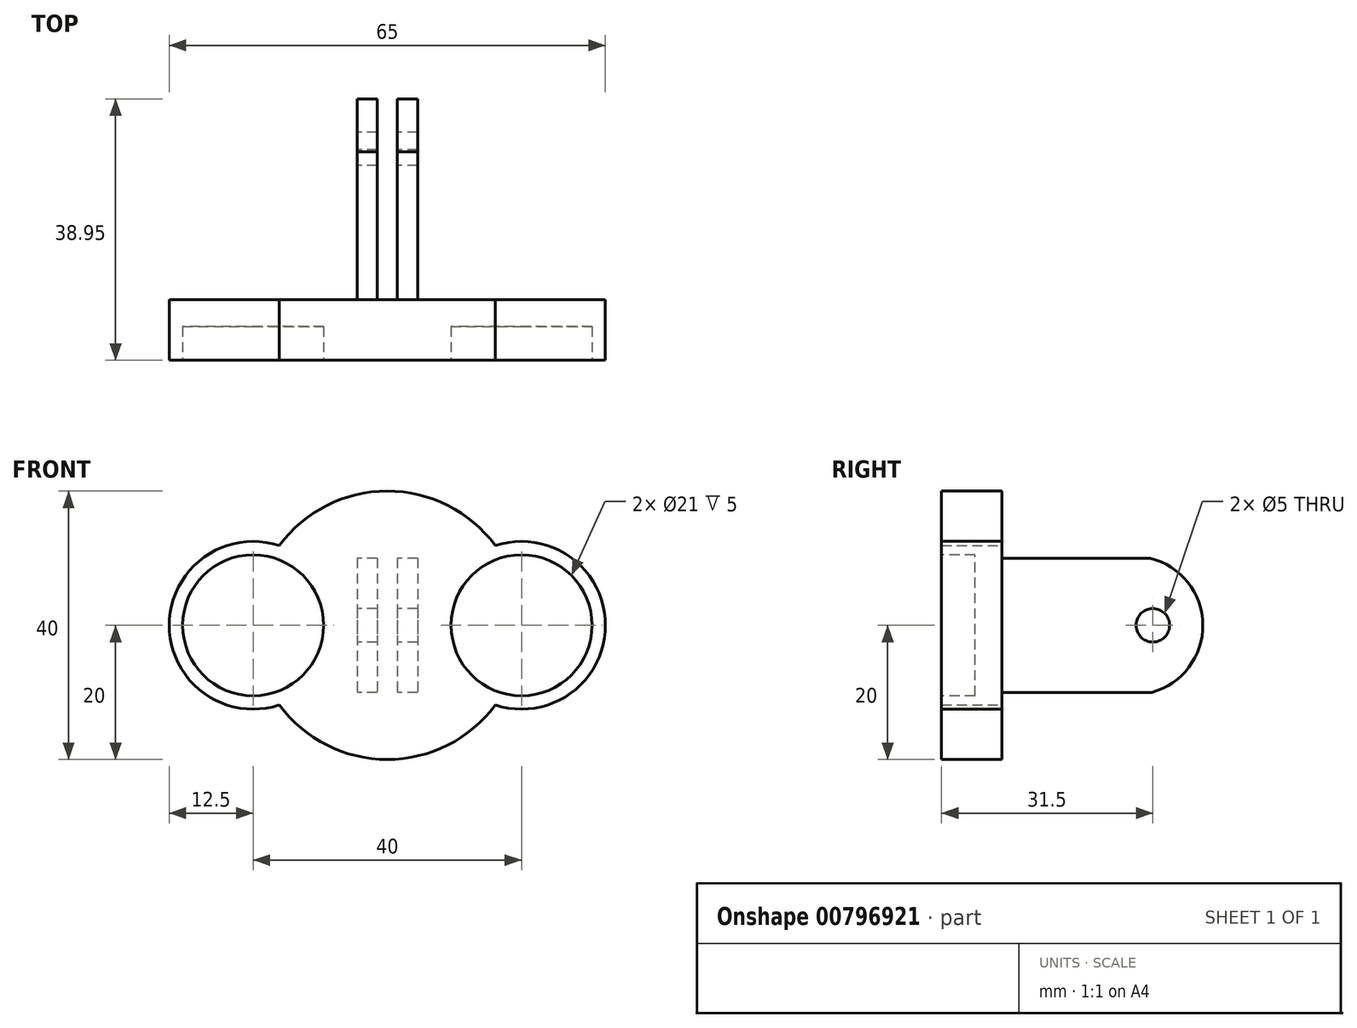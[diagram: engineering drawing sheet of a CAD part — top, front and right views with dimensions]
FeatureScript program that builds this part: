
annotation { "Feature Type Name" : "Feature", "Feature Type Description" : "" }
export const myFeature = defineFeature(function(context is Context, id is Id, definition is map)
    precondition{}
    {
        {
            var Q0;
            Q0=qCreatedBy(makeId("Front.planeOp"),FACE);
            var sketch = newSketch(context, id + "F0", { "sketchPlane" : qUnion([Q0])});
            skCircle(sketch, "E0", {"center": v(0, 0) * mm, "radius": 20 * mm});
            skCircle(sketch, "E1", {"center": v(-20, 0) * mm, "radius": 12.5 * mm});
            skCircle(sketch, "E2", {"center": v(20, 0) * mm, "radius": 12.5 * mm});
            skSolve(sketch);
        }
        {
            var Q0;
            Q0=qSketchRegion(id+"F0",true);
            extrude(context, id + "F1", {"entities" : qUnion([Q0]), "depth" : 9 * mm, "offsetDistance" : 25 * mm});
        }
        {
            var Q0;
            Q0=makeQuery(id+"F1.opExtrude","CAP_FACE",FACE,{"disambiguationData":[OSD([sQuery(id+"F0.wireOp",EDGE,"E0")])],"isStart":true});
            var sketch = newSketch(context, id + "F2", { "sketchPlane" : qUnion([Q0])});
            skLineSegment(sketch, "E3.bottom", {"start": v(-4.5, 10) * mm, "end": v(-1.5, 10) * mm});
            skLineSegment(sketch, "E3.top", {"start": v(-4.5, -10) * mm, "end": v(-1.5, -10) * mm});
            skLineSegment(sketch, "E3.left", {"start": v(-4.5, 10) * mm, "end": v(-4.5, -10) * mm});
            skLineSegment(sketch, "E3.right", {"start": v(-1.5, 10) * mm, "end": v(-1.5, -10) * mm});
            skLineSegment(sketch, "E4.bottom", {"start": v(1.5, 10) * mm, "end": v(4.5, 10) * mm});
            skLineSegment(sketch, "E4.top", {"start": v(1.5, -10) * mm, "end": v(4.5, -10) * mm});
            skLineSegment(sketch, "E4.left", {"start": v(1.5, 10) * mm, "end": v(1.5, -10) * mm});
            skLineSegment(sketch, "E4.right", {"start": v(4.5, 10) * mm, "end": v(4.5, -10) * mm});
            skSolve(sketch);
        }
        {
            var Q0;
            Q0=qSketchRegion(id+"F2",true);
            extrude(context, id + "F3", {"entities" : qUnion([Q0]), "operationType" : NewBodyOperationType.ADD, "depth" : 30 * mm, "offsetDistance" : 25 * mm});
        }
        {
            var Q0;
            Q0=makeQuery(id+"F3.opExtrude","SWEPT_FACE",FACE,{"disambiguationData":[OSD([sQuery(id+"F2.wireOp",EDGE,"E4.right")])]});
            var sketch = newSketch(context, id + "F4", { "sketchPlane" : qUnion([Q0])});
            skCircle(sketch, "E5", {"center": v(-22.5, 0) * mm, "radius": 2.5 * mm});
            skSolve(sketch);
        }
        {
            var Q0;
            Q0=qSketchRegion(id+"F4",true);
            extrude(context, id + "F5", {"entities" : qUnion([Q0]), "operationType" : NewBodyOperationType.REMOVE, "oppositeDirection" : true, "depth" : 10 * mm, "offsetDistance" : 25 * mm});
        }
        {
            var Q0;
            Q0=makeQuery(id+"F3.opExtrude","SWEPT_FACE",FACE,{"disambiguationData":[OSD([sQuery(id+"F2.wireOp",EDGE,"E4.right")])]});
            var sketch = newSketch(context, id + "F6", { "sketchPlane" : qUnion([Q0])});
            skArc(sketch, "E6", {"start": v(-22.08, 10) * mm, "mid": v(-29.95, 0.12) * mm, "end": v(-22.38, -10) * mm});
            skLineSegment(sketch, "E7", {"start": v(-22.08, 10) * mm, "end": v(-30, 10) * mm});
            skLineSegment(sketch, "E8", {"start": v(-30, 10) * mm, "end": v(-30, -10) * mm});
            skLineSegment(sketch, "E9", {"start": v(-30, -10) * mm, "end": v(-22.38, -10) * mm});
            skSolve(sketch);
        }
        {
            var Q0;
            Q0=makeQuery(id+"F6.imprint","IMPRINT",FACE,{"disambiguationData":[TD([[makeQuery(id+"F6.imprint","IMPRINT",EDGE,{"derivedFrom":sQuery(id+"F6.wireOp",EDGE,"E6")}),-1.0]])]});
            extrude(context, id + "F7", {"entities" : qUnion([Q0]), "operationType" : NewBodyOperationType.REMOVE, "oppositeDirection" : true, "depth" : 10 * mm, "offsetDistance" : 25 * mm});
        }
        {
            var Q0;
            Q0=makeQuery(id+"F1.opExtrude","CAP_FACE",FACE,{"disambiguationData":[OSD([sQuery(id+"F0.wireOp",EDGE,"E0"),sQuery(id+"F0.wireOp",EDGE,"E1"),sQuery(id+"F0.wireOp",EDGE,"E2")])],"isStart":false});
            var sketch = newSketch(context, id + "F8", { "sketchPlane" : qUnion([Q0])});
            skCircle(sketch, "E10", {"center": v(-20, 0) * mm, "radius": 10.5 * mm});
            skCircle(sketch, "E11", {"center": v(20, 0) * mm, "radius": 10.5 * mm});
            skSolve(sketch);
        }
        {
            var Q0;
            Q0 = qSketchRegion(id + "F8", true);
            extrude(context, id + "F9", {"entities" : qUnion([Q0]), "operationType" : NewBodyOperationType.REMOVE, "oppositeDirection" : true, "depth" : 5 * mm, "offsetDistance" : 25 * mm});
        }
    });
